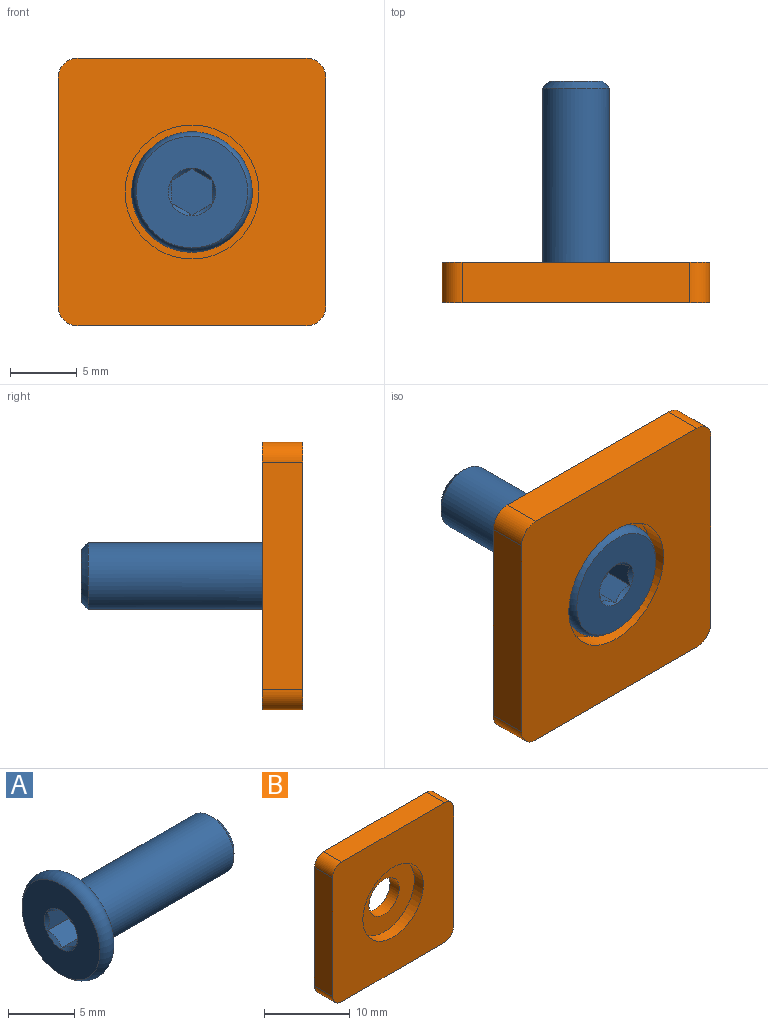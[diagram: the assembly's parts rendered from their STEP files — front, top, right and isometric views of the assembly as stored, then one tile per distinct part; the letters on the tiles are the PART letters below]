
ASSEMBLY  parts=2 mates=1
PART A: 14 faces, bbox 16.8x9.7x9.7 mm
  f0: cone r=1.78mm half-angle=45deg, axis (-1,0,0), area 3.1mm2, adj f5,f8,f9,f10,f11,f12,f13
  f1: torus R=3.5mm, axis (1,0,0), area 46.7mm2, adj f5,f6
  f2: cone r=2mm half-angle=45deg, axis (-1,0,0), area 10mm2, adj f3,f4
  f3: cylinder r=2.5mm len=14.5mm, axis (1,0,0), area 227.8mm2, adj f2,f6
  f4: plane 4x4mm, normal (1,0,0), area 12.6mm2, adj f2
  f5: plane 8.32x8.32mm, normal (-1,0,0), area 44.4mm2, adj f0,f1
  f6: plane 8.32x8.32mm, normal (1,0,0), area 34.8mm2, adj f1,f3
  f7: plane 3.46x3mm, normal (-1,0,0), area 7.8mm2, adj f8,f9,f10,f11,f12,f13
  f8: plane 2.25x1.5mm, normal (0,-0.5,-0.87), area 3.6mm2, adj f0,f7,f9,f13
  f9: plane 2.25x1.73mm, normal (0,-1,0), area 3.6mm2, adj f0,f7,f8,f10
  f10: plane 2.25x1.5mm, normal (0,-0.5,0.87), area 3.6mm2, adj f0,f7,f9,f11
  f11: plane 2.25x1.5mm, normal (0,0.5,0.87), area 3.6mm2, adj f0,f7,f10,f12
  f12: plane 2.25x1.73mm, normal (0,1,0), area 3.6mm2, adj f0,f7,f11,f13
  f13: plane 2.25x1.5mm, normal (0,0.5,-0.87), area 3.6mm2, adj f0,f7,f8,f12
PART B: 13 faces, bbox 20x3x20 mm
  f0: cylinder r=5mm len=10mm, axis (0,-1,0), area 47.1mm2, adj f2,f8
  f1: cylinder r=2.5mm len=5mm, axis (0,1,0), area 23.6mm2, adj f3,f8
  f2: plane 20x20mm, normal (0,-1,0), area 319.5mm2, adj f0,f4,f5,f6,f7,f9,f10,f11
  f3: plane 20x20mm, normal (0,1,0), area 378.4mm2, adj f1,f4,f5,f6,f7,f9,f10,f11
  f4: plane 17x3mm, normal (-1,0,0), area 51mm2, adj f2,f3,f11,f12
  f5: plane 17x3mm, normal (0,0,-1), area 51mm2, adj f2,f3,f10,f11
  f6: plane 17x3mm, normal (1,0,0), area 51mm2, adj f2,f3,f9,f10
  f7: plane 17x3mm, normal (0,0,1), area 51mm2, adj f2,f3,f9,f12
  f8: plane 10x10mm, normal (0,-1,0), area 58.9mm2, adj f0,f1
  f9: cylinder r=1.5mm len=3mm, axis (0,1,0), area 7.1mm2, adj f2,f3,f6,f7
  f10: cylinder r=1.5mm len=3mm, axis (0,1,0), area 7.1mm2, adj f2,f3,f5,f6
  f11: cylinder r=1.5mm len=3mm, axis (0,1,0), area 7.1mm2, adj f2,f3,f4,f5
  f12: cylinder r=1.5mm len=3mm, axis (0,1,0), area 7.1mm2, adj f2,f3,f4,f7
PLACE A rot(axis=(-0.71,-0.71,0),180deg) t=(0,6.5,0)mm
PLACE B at identity fixed
MATE fastened A.f0 <-> B.f0  axis (0,1,0) through (0,-1.5,0)mm
